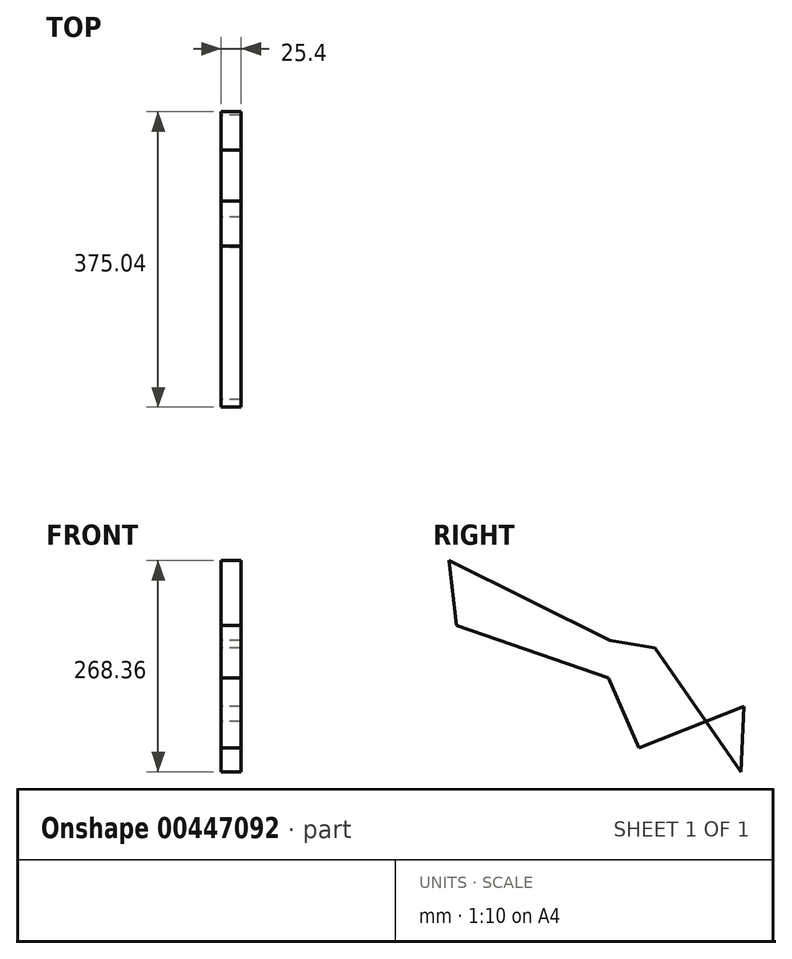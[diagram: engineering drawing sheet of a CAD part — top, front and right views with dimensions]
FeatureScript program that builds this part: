
annotation { "Feature Type Name" : "Feature", "Feature Type Description" : "" }
export const myFeature = defineFeature(function(context is Context, id is Id, definition is map)
    precondition{}
    {
        {
            var Q0;
            Q0=qCreatedBy(makeId("Right.planeOp"),FACE);
            var sketch = newSketch(context, id + "F0", { "sketchPlane" : qUnion([Q0])});
            skLineSegment(sketch, "E0", {"start": v(126.46, 0) * mm, "end": v(0, 0) * mm});
            skLineSegment(sketch, "E1", {"start": v(0, 0) * mm, "end": v(126.46, 0) * mm});
            skLineSegment(sketch, "E2", {"start": v(203.54, -74.77) * mm, "end": v(47.64, -48.32) * mm});
            skLineSegment(sketch, "E3", {"start": v(47.64, -48.32) * mm, "end": v(-156.77, 52.88) * mm});
            skLineSegment(sketch, "E4", {"start": v(-156.77, 52.88) * mm, "end": v(-147.24, -29.9) * mm});
            skLineSegment(sketch, "E5", {"start": v(-147.24, -29.9) * mm, "end": v(45.9, -96.46) * mm});
            skLineSegment(sketch, "E6", {"start": v(45.9, -96.46) * mm, "end": v(84.88, -184.96) * mm});
            skLineSegment(sketch, "E7", {"start": v(84.88, -184.96) * mm, "end": v(218.27, -132.64) * mm});
            skLineSegment(sketch, "E8", {"start": v(218.27, -132.64) * mm, "end": v(213.93, -215.48) * mm});
            skLineSegment(sketch, "E9", {"start": v(213.93, -215.48) * mm, "end": v(36.38, 41.32) * mm});
            skLineSegment(sketch, "E10", {"start": v(36.38, 41.32) * mm, "end": v(-163.7, 139.36) * mm});
            skLineSegment(sketch, "E11", {"start": v(-163.7, 139.36) * mm, "end": v(-58.03, 47.02) * mm});
            skSolve(sketch);
        }
        {
            var Q0;
            Q0 = qSketchRegion(id + "F0", true);
            extrude(context, id + "F1", {"entities" : qUnion([Q0]), "depth" : 25.4 * mm});
        }
    });
